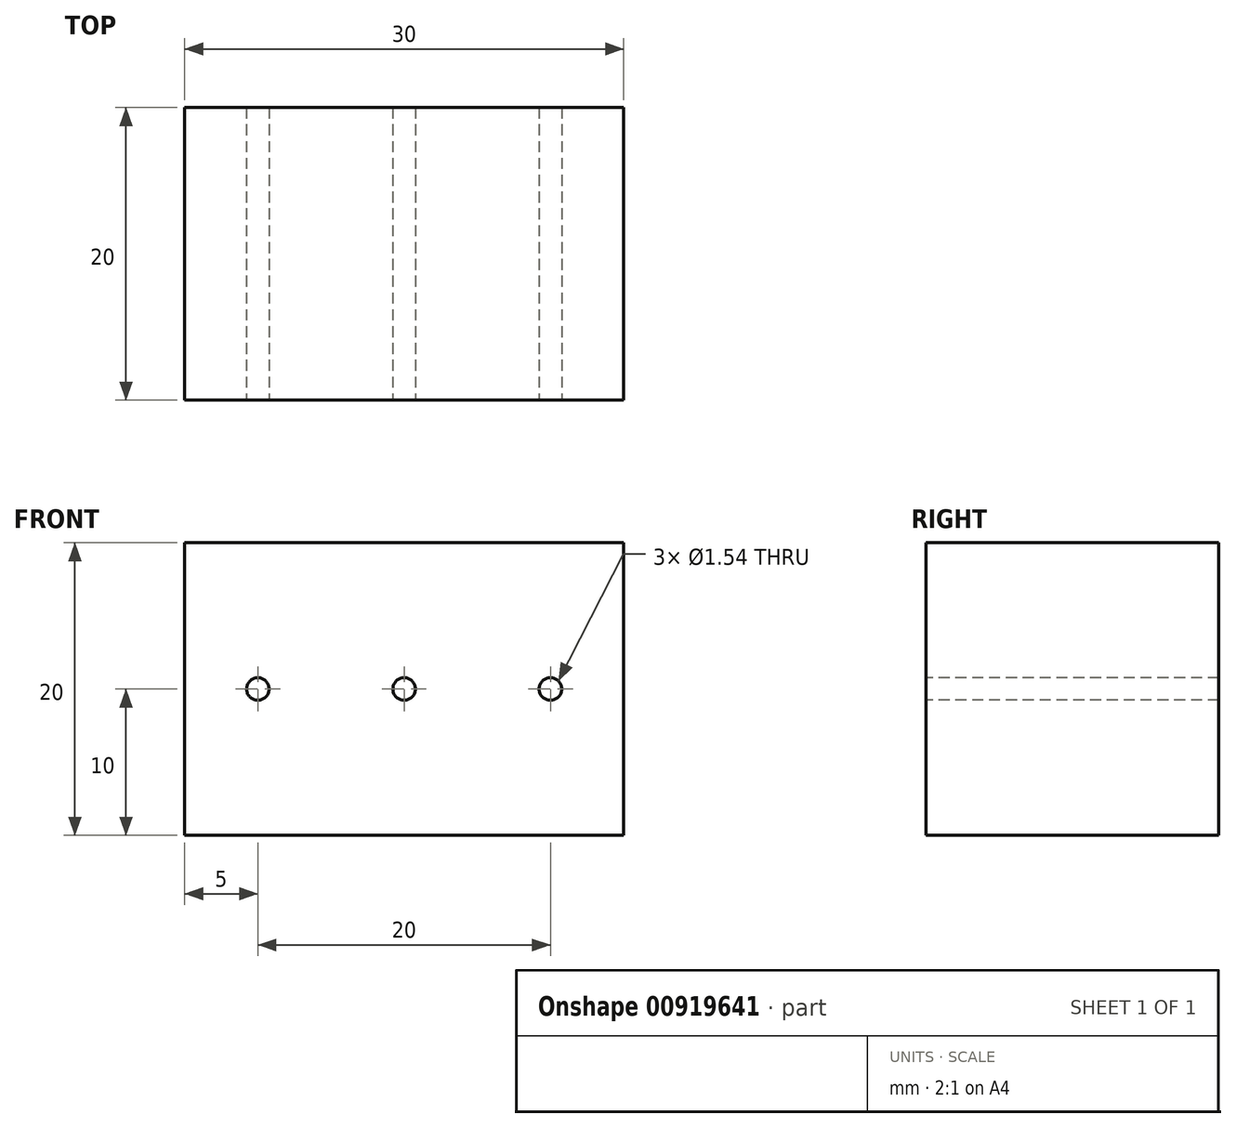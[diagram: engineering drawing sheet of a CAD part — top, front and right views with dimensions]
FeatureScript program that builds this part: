
annotation { "Feature Type Name" : "Feature", "Feature Type Description" : "" }
export const myFeature = defineFeature(function(context is Context, id is Id, definition is map)
    precondition{}
    {
        {
            var Q0;
            Q0=qCreatedBy(makeId("Front.planeOp"),FACE);
            var sketch = newSketch(context, id + "F0", { "sketchPlane" : qUnion([Q0])});
            skLineSegment(sketch, "E0.bottom", {"start": v(15, -10) * mm, "end": v(-15, -10) * mm});
            skLineSegment(sketch, "E0.top", {"start": v(15, 10) * mm, "end": v(-15, 10) * mm});
            skLineSegment(sketch, "E0.left", {"start": v(15, -10) * mm, "end": v(15, 10) * mm});
            skLineSegment(sketch, "E0.right", {"start": v(-15, -10) * mm, "end": v(-15, 10) * mm});
            skPoint(sketch, "E0.middle", {"position": v(0, 0) * mm});
            skSolve(sketch);
        }
        {
            var Q0;
            Q0 = qSketchRegion(id + "F0", true);
            extrude(context, id + "F1", {"entities" : qUnion([Q0]), "endBound" : BoundingType.SYMMETRIC, "depth" : 20 * mm, "offsetDistance" : 25.4 * mm});
        }
        {
            var Q0;
            Q0=makeQuery(id+"F1.opExtrude","CAP_FACE",FACE,{"disambiguationData":[OSD([sQuery(id+"F0.wireOp",EDGE,"E0.bottom"),sQuery(id+"F0.wireOp",EDGE,"E0.top"),sQuery(id+"F0.wireOp",EDGE,"E0.left"),sQuery(id+"F0.wireOp",EDGE,"E0.right")])],"isStart":false});
            var sketch = newSketch(context, id + "F2", { "sketchPlane" : qUnion([Q0])});
            skPoint(sketch, "E1", {"position": v(-10, 0) * mm});
            skPoint(sketch, "E2", {"position": v(0, 0) * mm});
            skPoint(sketch, "E3.MirrorP", {"position": v(10, 0) * mm});
            skSolve(sketch);
        }
        {
            var Q0;
            Q0=sQuery(id+"F2.wireOp",VERTEX,"E1");
            var Q1;
            Q1=sQuery(id+"F2.wireOp",VERTEX,"E2");
            var Q2;
            Q2=sQuery(id+"F2.wireOp",VERTEX,"E3.MirrorP");
            var Q3;
            Q3=makeQuery(id+"F1.opExtrude","SWEPT_BODY",BODY,{"disambiguationData":[OSD([sQuery(id+"F0.wireOp",EDGE,"E0.bottom"),sQuery(id+"F0.wireOp",EDGE,"E0.top"),sQuery(id+"F0.wireOp",EDGE,"E0.left"),sQuery(id+"F0.wireOp",EDGE,"E0.right")])]});
            hole(context, id + "F3", {"style" : HoleStyle.SIMPLE, "endStyle" : HoleEndStyle.THROUGH, "holeDiameter" : 1.54 * mm, "majorDiameter" : 6.35 * mm, "isTappedThrough" : true, "tappedDepth" : 12.7 * mm, "tapClearance" : 3, "startFromSketch" : true, "locations" : qUnion([Q0, Q1, Q2]), "scope" : qUnion([Q3])});
        }
    });
